# Revit family: Drain_Floor_9_Inch-Zurn -Z511-Heavy-Duty
name_source: partatom
category: Plumbing Fixtures
units: mm (PartAtom-declared; Revit-internal decimal feet)

## family parameters
Always vertical = Yes
Cut with Voids When Loaded = No
Maintain Annotation Orientation = No
OmniClass Number = 23.70.50.21.24.14
OmniClass Title = Deck Waste Water Drains
Part Type = Normal
Room Calculation Point = No
Round Connector Dimension = Use Radius
Shared = No
Work Plane-Based = No

## types (18) — shared parameters
Approx. Weight (Lbs) = 40 "
Assembly Code = D2030300
CW Connection = No
Default Elevation = 20 "
Description = 9 [229]  DIAMETER HEAVY-DUTY DRAIN W/INTEGRAL TRAP PRIMER CONNECTION
Grate Open Area = 18.00 in²
HW Connection = No
Manufacturer = Zurn Water, LLC
Manufacurer Brand = Zurn
Modified Date = 11/19/2025
Product Documentation Link = https://files.zurn.com
Product Page URL = https://www.zurn.com
Product data url = https://www.bimobject.com
URL = www.zurn.com
Vent Connection = No
WFU = 1
Waste Connection = Yes
zero-valued in all types: CWFU, HWFU

## per-type parameters (varying)
| type | "E" Body Height | FrameHeight | Grate Model line radius | Model | Pipe Size "A" (Inner Diameter) | Pipe Size "A" (Nominal Radius) | Pipe Size "A" (Outer Diameter) | Pipe Size "A"(Innr Radius) | Pipe Size "A"(Nominal Diameter) | Pipe Size "A"(Outer Radius) | TopHeight | Type Comments |
| Z511-3 IC | 7.625 " | 2 " | 4.5 " | Z511 | 3.068 " | 1.5 " | 3.5 " | 1.534 " | 3 " | 1.75 " | No | Z511 With 3 Inch Inside Caulk Outlet |
| Z511-4 IC | 7.625 " | 2 " | 4.5 " | Z511 | 4.026 " | 2 " | 4.5 " | 2.013 " | 4 " | 2.25 " | No | Z511 With 4 Inch Inside Caulk Outlet |
| Z511-3 IG | 7.625 " | 2 " | 4.5 " | Z511 | 3.068 " | 1.5 " | 3.5 " | 1.534 " | 3 " | 1.75 " | No | Z511 With 3 Inch Inside Gasket Outlet |
| Z511-4 IG | 7.625 " | 2 " | 4.5 " | Z511 | 4.026 " | 2 " | 4.5 " | 2.013 " | 4 " | 2.25 " | No | Z511 With 4 Inch Inside Gasket Outlet |
| Z511-3 IP | 7.625 " | 2 " | 4.5 " | Z511 | 3.068 " | 1.5 " | 3.5 " | 1.534 " | 3 " | 1.75 " | No | Z511 With 3 Inch Threaded Outlet |
| Z511-4 IP | 7.625 " | 2 " | 4.5 " | Z511 | 4.026 " | 2 " | 4.5 " | 2.013 " | 4 " | 2.25 " | No | Z511 With 3 Inch Threaded Outlet |
| Z511-2 NL | 6.875 " | 2 " | 4.5 " | Z511 | 2.067 " | 1 " | 2.375 " | 1.034 " | 2 " | 1.188 " | No | Z511 With 2 Inch Neo-Loc Outlet |
| Z511-3 NL | 6.875 " | 2 " | 4.5 " | Z511 | 3.068 " | 1.5 " | 3.5 " | 1.534 " | 3 " | 1.75 " | No | Z511 With 3 Inch Neo-Loc Outlet |
| Z511-4 NL | 6.875 " | 2 " | 4.5 " | Z511 | 4.026 " | 2 " | 4.5 " | 2.013 " | 4 " | 2.25 " | No | Z511 With 4 Inch Neo-Loc Outlet |
| ZN511-3 IC | 7.625 " | 2.188 " | 4.594 " | ZN511 | 3.068 " | 1.5 " | 3.5 " | 1.534 " | 3 " | 1.75 " | Yes | ZN511 With 3 Inch Inside Caulk Outlet |
| ZN511-4 IC | 7.625 " | 2.188 " | 4.594 " | ZN511 | 4.026 " | 2 " | 4.5 " | 2.013 " | 4 " | 2.25 " | Yes | ZN511 With 4 Inch Inside Caulk Outlet |
| ZN511-3 IG | 7.625 " | 2.188 " | 4.594 " | ZN511 | 3.068 " | 1.5 " | 3.5 " | 1.534 " | 3 " | 1.75 " | Yes | ZN511 With 3 Inch Inside Gasket Outlet |
| ZN511-4 IG | 7.625 " | 2.188 " | 4.594 " | ZN511 | 4.026 " | 2 " | 4.5 " | 2.013 " | 4 " | 2.25 " | Yes | ZN511 With 4 Inch Inside Gasket Outlet |
| ZN511-3 IP | 7.625 " | 2.188 " | 4.594 " | ZN511 | 3.068 " | 1.5 " | 3.5 " | 1.534 " | 3 " | 1.75 " | Yes | ZN511 With 3 Inch Threaded Outlet |
| ZN511-4 IP | 7.625 " | 2.188 " | 4.594 " | ZN511 | 4.026 " | 2 " | 4.5 " | 2.013 " | 4 " | 2.25 " | Yes | ZN511 With 3 Inch Threaded Outlet |
| ZN511-2 NL | 6.875 " | 2.188 " | 4.594 " | ZN511 | 2.067 " | 1 " | 2.375 " | 1.034 " | 2 " | 1.188 " | Yes | ZN511 With 2 Inch Neo-Loc Outlet |
| ZN511-3 NL | 6.875 " | 2.188 " | 4.594 " | ZN511 | 3.068 " | 1.5 " | 3.5 " | 1.534 " | 3 " | 1.75 " | Yes | ZN511 With 3 Inch Neo-Loc Outlet |
| ZN511-4 NL | 6.875 " | 2.188 " | 4.594 " | ZN511 | 4.026 " | 2 " | 4.5 " | 2.013 " | 4 " | 2.25 " | Yes | ZN511 With 4 Inch Neo-Loc Outlet |

## geometry (parser evidence)
native form markers: Sweep x5
no freeform markers — native parametric forms only
